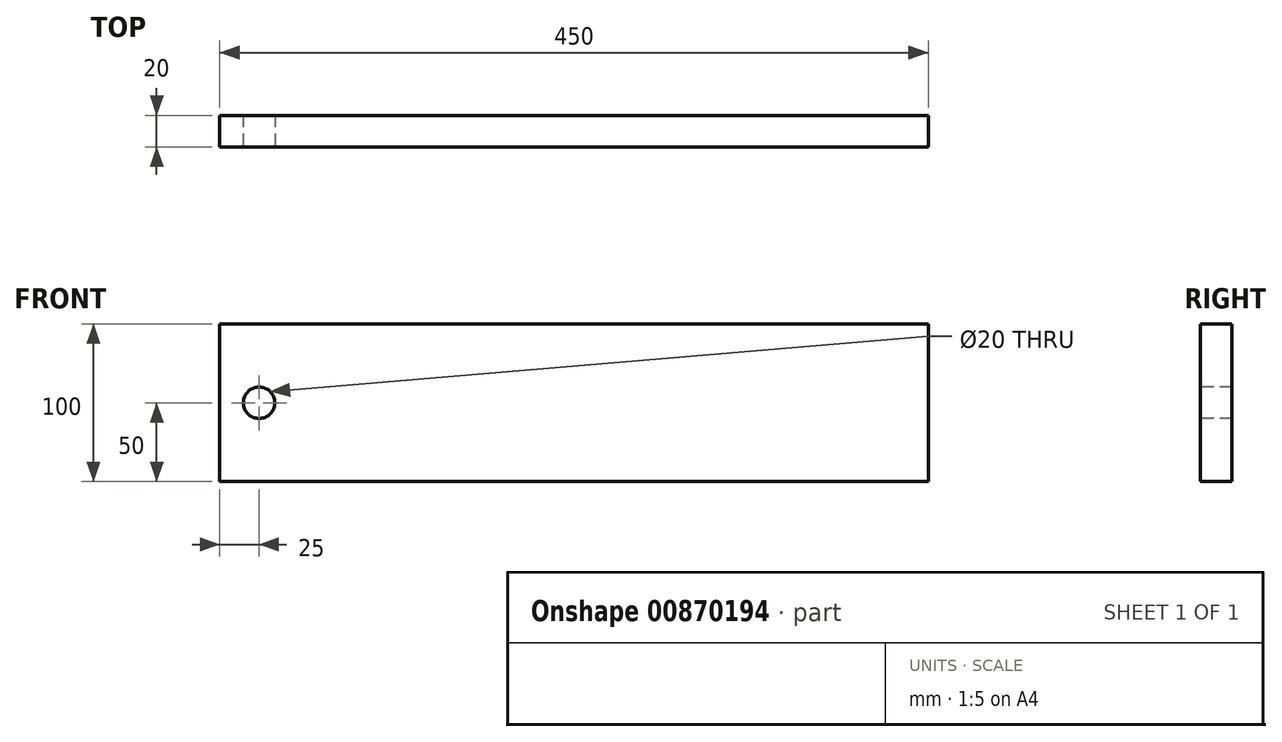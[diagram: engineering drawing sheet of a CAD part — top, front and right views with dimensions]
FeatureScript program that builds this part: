
annotation { "Feature Type Name" : "Feature", "Feature Type Description" : "" }
export const myFeature = defineFeature(function(context is Context, id is Id, definition is map)
    precondition{}
    {
        {
            var Q0;
            Q0=qCreatedBy(makeId("Front.planeOp"),FACE);
            var sketch = newSketch(context, id + "F0", { "sketchPlane" : qUnion([Q0])});
            skLineSegment(sketch, "E0.bottom", {"start": v(225, -50) * mm, "end": v(-225, -50) * mm});
            skLineSegment(sketch, "E0.top", {"start": v(225, 50) * mm, "end": v(-225, 50) * mm});
            skLineSegment(sketch, "E0.left", {"start": v(225, -50) * mm, "end": v(225, 50) * mm});
            skLineSegment(sketch, "E0.right", {"start": v(-225, -50) * mm, "end": v(-225, 50) * mm});
            skPoint(sketch, "E0.middle", {"position": v(0, 0) * mm});
            skSolve(sketch);
        }
        {
            var Q0;
            Q0=makeQuery(id+"F0.imprint","IMPRINT",FACE,{"disambiguationData":[TD([[makeQuery(id+"F0.imprint","IMPRINT",EDGE,{"derivedFrom":sQuery(id+"F0.wireOp",EDGE,"E0.bottom")}),-1.0]])]});
            extrude(context, id + "F1", {"entities" : qUnion([Q0]), "endBound" : BoundingType.SYMMETRIC, "depth" : 20 * mm, "offsetDistance" : 25 * mm});
        }
        {
            var Q0;
            Q0=makeQuery(id+"F1.opExtrude","CAP_FACE",FACE,{"disambiguationData":[OSD([sQuery(id+"F0.wireOp",EDGE,"E0.bottom"),sQuery(id+"F0.wireOp",EDGE,"E0.top"),sQuery(id+"F0.wireOp",EDGE,"E0.left"),sQuery(id+"F0.wireOp",EDGE,"E0.right")])],"isStart":false});
            var sketch = newSketch(context, id + "F2", { "sketchPlane" : qUnion([Q0])});
            skCircle(sketch, "E1", {"center": v(-200, 0) * mm, "radius": 10 * mm});
            skPoint(sketch, "E1.centerSnap0", {"position": v(-225, 0) * mm});
            skSolve(sketch);
        }
        {
            var Q0;
            Q0=makeQuery(id+"F2.imprint","IMPRINT",FACE,{"disambiguationData":[TD([[makeQuery(id+"F2.imprint","IMPRINT",EDGE,{"derivedFrom":sQuery(id+"F2.wireOp",EDGE,"E1")}),1.0]])]});
            extrude(context, id + "F3", {"entities" : qUnion([Q0]), "operationType" : NewBodyOperationType.REMOVE, "endBound" : BoundingType.THROUGH_ALL, "oppositeDirection" : true, "depth" : 25 * mm, "offsetDistance" : 25 * mm});
        }
    });
